# Revit family: Faucet-Kitchen-KOHLER-Components-K-28267BR
name_source: partatom
category: Plumbing Fixtures
units: mm (PartAtom-declared; Revit-internal decimal feet)

## family parameters
Cut with Voids When Loaded = No
Host = Face
OmniClass Number = 23.31.11.00
OmniClass Title = Faucets
Part Type = Normal
Room Calculation Point = No
Round Connector Dimension = Use Diameter
Shared = No

## types (4) — shared parameters
ADA Compliant = No
Assembly Code = D2010
CW Connection = Yes
Cold Water Inlet = Cold Water Inlet
Date Modified = 08/25/2023
Default Elevation = 36"
Description = SEMIPRO
Drain Included = No
Flow Rate = 2 GPM
HW Connection = Yes
Handle Clearance = 2 13/16"
Height = 23"
Hot Water Inlet = Hot Water Inlet
Length = 9"
Manufacturer = Kohler Co.
Master Format 2014 = 22 41 39
Master Format 2014 Name = Residential Faucets, Supplies, and Trim
Material = Premiun Metal Construction
Pressure = 60.00 psi
Product Name = Components
Spout Reach = 9"
URL = https://br.kohler.com
Vent Connection = No
Waste Connection = No
Waste Water Outlet = Waste Water Outlet
WaterSense Certified = No
Width = 2 5/16"

## per-type parameters (varying)
| type | Finish | Model | Secondary Finish | Type |
| 2MB-Vibrant Brushed Moderne Brass | Kohler-Metal-2MB-Vibrant_Brushed_Moderne_Brass | K-28267BR-2MB | Plastic-Pantone-PQ-194205-TCX | 1 |
| BL-Matte Black | Kohler-Metal-BL-Matte_Black | K-28267BR-BL | Plastic-Pantone-Black_C | 2 |
| CP-Polished Chrome | Kohler-Metal-CP-Polished_Chrome | K-28267BR-CP | Plastic-Pantone-PQ-194205-TCX | 3 |
| VS-Vibrant Stainless | Kohler-Metal-VS-Vibrant_Stainless | K-28267BR-VS | Plastic-Pantone-PQ-194205-TCX | 4 |

## geometry (parser evidence)
native form markers: Sweep x5
no freeform markers — native parametric forms only
